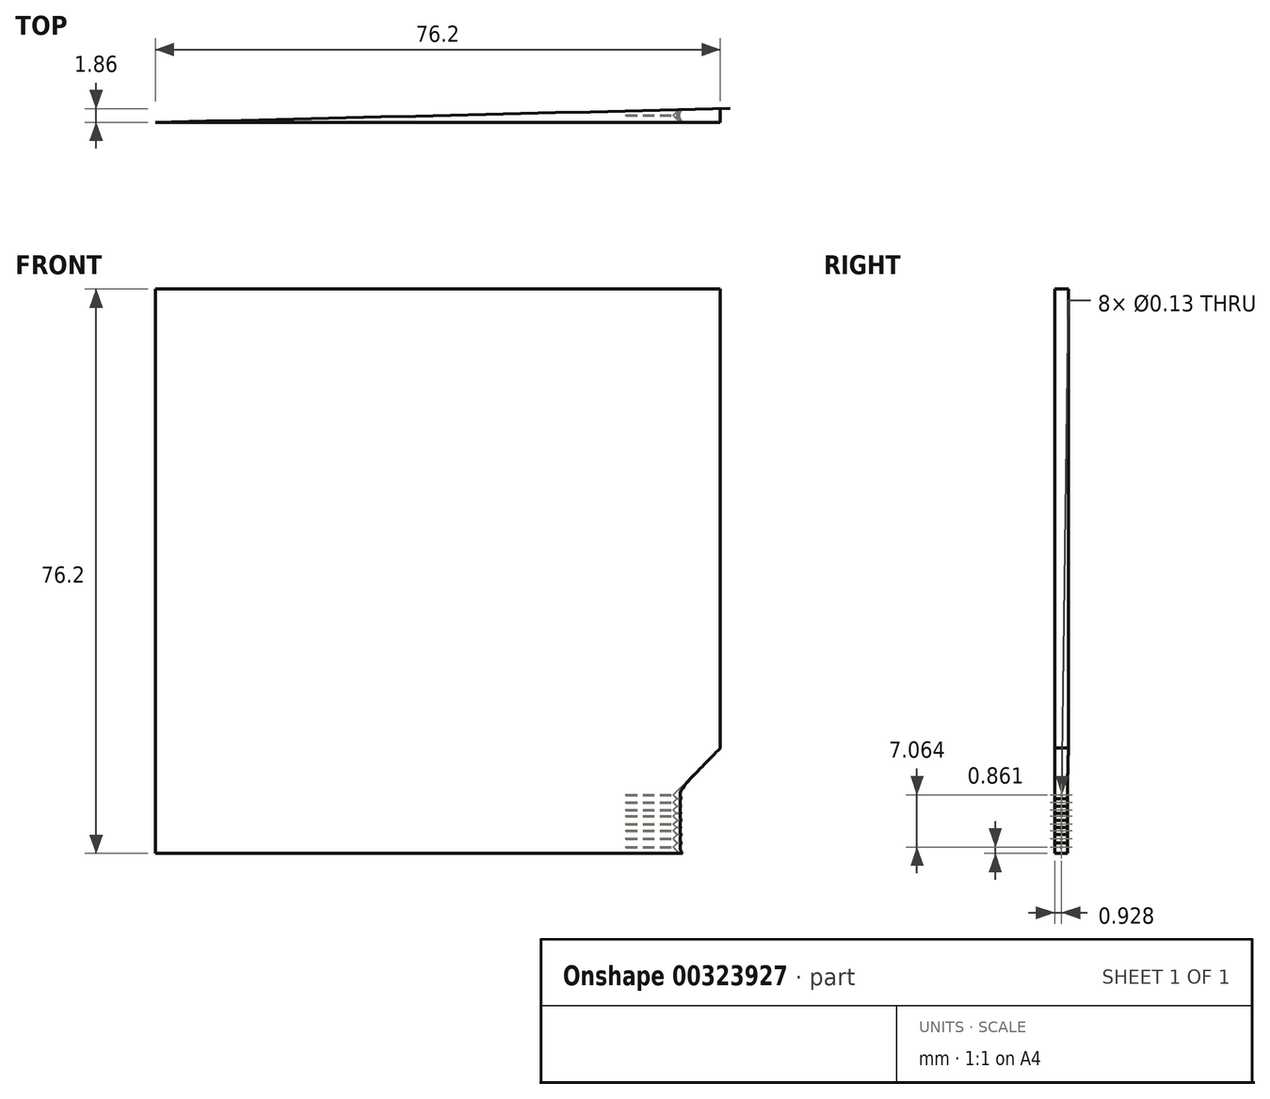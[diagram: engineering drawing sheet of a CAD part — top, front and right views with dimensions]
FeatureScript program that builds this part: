
annotation { "Feature Type Name" : "Feature", "Feature Type Description" : "" }
export const myFeature = defineFeature(function(context is Context, id is Id, definition is map)
    precondition{}
    {
        {
            var Q0;
            Q0=qCreatedBy(makeId("Top.planeOp"),FACE);
            var sketch = newSketch(context, id + "F0", { "sketchPlane" : qUnion([Q0])});
            skLineSegment(sketch, "E0.bottom", {"start": v(-38.1, 38.1) * mm, "end": v(38.1, 38.1) * mm});
            skLineSegment(sketch, "E0.top", {"start": v(-38.1, -38.1) * mm, "end": v(38.1, -38.1) * mm});
            skLineSegment(sketch, "E0.left", {"start": v(-38.1, 38.1) * mm, "end": v(-38.1, -38.1) * mm});
            skLineSegment(sketch, "E0.right", {"start": v(38.1, 38.1) * mm, "end": v(38.1, -38.1) * mm});
            skPoint(sketch, "E0.middle", {"position": v(0, 0) * mm});
            skSolve(sketch);
        }
        {
            var Q0;
            Q0=makeQuery(id+"F0.imprint","IMPRINT",FACE,{"disambiguationData":[TD([[makeQuery(id+"F0.imprint","IMPRINT",EDGE,{"derivedFrom":sQuery(id+"F0.wireOp",EDGE,"E0.bottom")}),-1.0]])]});
            extrude(context, id + "F1", {"entities" : qUnion([Q0]), "endBound" : BoundingType.SYMMETRIC, "depth" : 76.2 * mm});
        }
        {
            var Q0;
            Q0=makeQuery(id+"F1.opExtrude","SWEPT_EDGE",EDGE,{"disambiguationData":[OSD([sQuery(id+"F0.wireOp",EDGE,"E0.bottom"),sQuery(id+"F0.wireOp",EDGE,"E0.left")])]});
            fillet(context, id + "F2", {"entities" : qUnion([Q0]), "radius" : 254000 * mm, "tangentPropagation" : true, "allowEdgeOverflow" : false});
        }
        {
            var Q0;
            Q0=makeQuery(id+"F1.opExtrude","SWEPT_FACE",FACE,{"disambiguationData":[OSD([sQuery(id+"F0.wireOp",EDGE,"E0.right")])]});
            var sketch = newSketch(context, id + "F3", { "sketchPlane" : qUnion([Q0])});
            skLineSegment(sketch, "E1", {"start": v(-37.17, -38.1) * mm, "end": v(-37.17, 38.1) * mm, "construction": true});
            skPoint(sketch, "E2", {"position": v(-37.17, -37.24) * mm});
            skPoint(sketch, "E3", {"position": v(-37.17, -36.13) * mm});
            skPoint(sketch, "E4", {"position": v(-37.17, -35) * mm});
            skPoint(sketch, "E5", {"position": v(-37.17, -34.14) * mm});
            skPoint(sketch, "E6", {"position": v(-37.17, -33.06) * mm});
            skPoint(sketch, "E7", {"position": v(-37.17, -32.24) * mm});
            skPoint(sketch, "E8", {"position": v(-37.17, -31.21) * mm});
            skPoint(sketch, "E9", {"position": v(-37.17, -30.18) * mm});
            skSolve(sketch);
        }
        {
            var Q0;
            Q0=sQuery(id+"F3.wireOp",VERTEX,"E2");
            var Q1;
            Q1=sQuery(id+"F3.wireOp",VERTEX,"E3");
            var Q2;
            Q2=sQuery(id+"F3.wireOp",VERTEX,"E4");
            var Q3;
            Q3=sQuery(id+"F3.wireOp",VERTEX,"E5");
            var Q4;
            Q4=sQuery(id+"F3.wireOp",VERTEX,"E6");
            var Q5;
            Q5=sQuery(id+"F3.wireOp",VERTEX,"E7");
            var Q6;
            Q6=sQuery(id+"F3.wireOp",VERTEX,"E8");
            var Q7;
            Q7=sQuery(id+"F3.wireOp",VERTEX,"E9");
            var Q8;
            Q8=makeQuery(id+"F1.opExtrude","SWEPT_BODY",BODY,{"disambiguationData":[OSD([sQuery(id+"F0.wireOp",EDGE,"E0.bottom"),sQuery(id+"F0.wireOp",EDGE,"E0.top"),sQuery(id+"F0.wireOp",EDGE,"E0.left"),sQuery(id+"F0.wireOp",EDGE,"E0.right")])]});
            hole(context, id + "F4", {"style" : HoleStyle.C_SINK, "endStyle" : HoleEndStyle.BLIND, "holeDiameter" : 0.13 * mm, "cSinkDiameter" : 12.7 * mm, "cSinkAngle" : 90 * degree, "holeDepth" : 12.7 * mm, "tappedDepth" : 12.7 * mm, "tapClearance" : 3, "locations" : qUnion([Q0, Q1, Q2, Q3, Q4, Q5, Q6, Q7]), "scope" : qUnion([Q8])});
        }
    });
